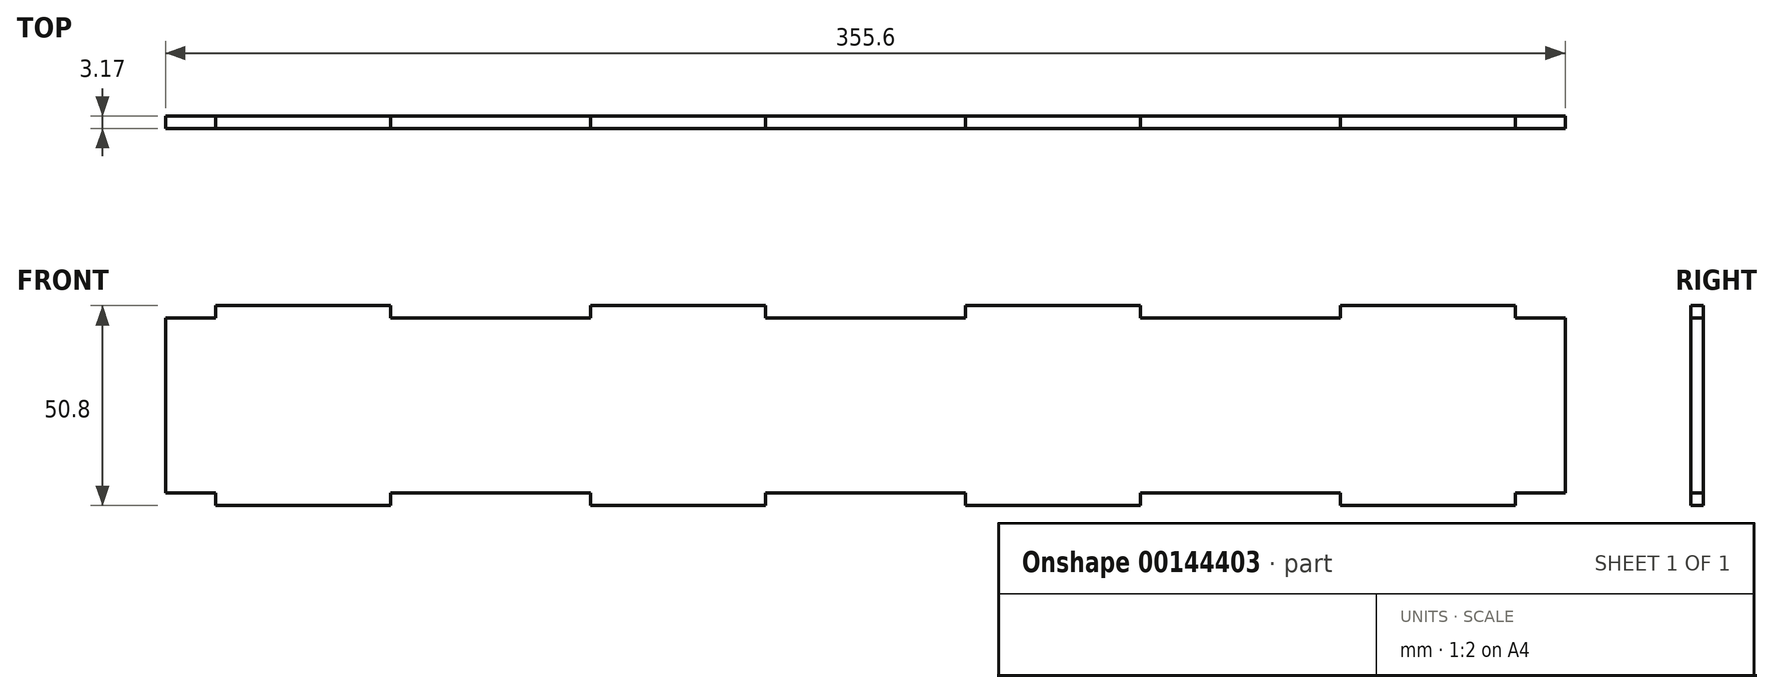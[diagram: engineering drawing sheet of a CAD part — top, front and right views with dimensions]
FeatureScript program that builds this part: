
annotation { "Feature Type Name" : "Feature", "Feature Type Description" : "" }
export const myFeature = defineFeature(function(context is Context, id is Id, definition is map)
    precondition{}
    {
        {
            var Q0;
            Q0=qCreatedBy(makeId("Front.planeOp"),FACE);
            var sketch = newSketch(context, id + "F0", { "sketchPlane" : qUnion([Q0])});
            skLineSegment(sketch, "E0", {"start": v(12.7, 0) * mm, "end": v(57.15, 0) * mm});
            skLineSegment(sketch, "E1", {"start": v(177.8, 3.18) * mm, "end": v(177.8, 47.62) * mm});
            skLineSegment(sketch, "E2", {"start": v(152.4, 50.8) * mm, "end": v(107.95, 50.8) * mm});
            skLineSegment(sketch, "E3", {"start": v(0, 47.62) * mm, "end": v(0, 3.18) * mm});
            skLineSegment(sketch, "E4.top", {"start": v(0, 47.62) * mm, "end": v(12.7, 47.62) * mm});
            skLineSegment(sketch, "E4.right", {"start": v(12.7, 50.8) * mm, "end": v(12.7, 47.62) * mm});
            skLineSegment(sketch, "E5.top", {"start": v(177.8, 47.62) * mm, "end": v(152.4, 47.62) * mm});
            skLineSegment(sketch, "E5.right", {"start": v(152.4, 50.8) * mm, "end": v(152.4, 47.62) * mm});
            skLineSegment(sketch, "E6.top", {"start": v(57.15, 47.62) * mm, "end": v(107.95, 47.62) * mm});
            skLineSegment(sketch, "E6.left", {"start": v(57.15, 50.8) * mm, "end": v(57.15, 47.62) * mm});
            skLineSegment(sketch, "E6.right", {"start": v(107.95, 50.8) * mm, "end": v(107.95, 47.62) * mm});
            skLineSegment(sketch, "E7", {"start": v(0, 25.4) * mm, "end": v(177.8, 25.4) * mm});
            skLineSegment(sketch, "E8.MirrorCS", {"start": v(0, 3.17) * mm, "end": v(12.7, 3.17) * mm});
            skLineSegment(sketch, "E9.MirrorCS", {"start": v(12.7, 0) * mm, "end": v(12.7, 3.18) * mm});
            skLineSegment(sketch, "E10.MirrorCS", {"start": v(57.15, 0) * mm, "end": v(57.15, 3.17) * mm});
            skLineSegment(sketch, "E11.MirrorCS", {"start": v(57.15, 3.17) * mm, "end": v(107.95, 3.18) * mm});
            skLineSegment(sketch, "E12.MirrorCS", {"start": v(107.95, 0) * mm, "end": v(107.95, 3.17) * mm});
            skLineSegment(sketch, "E13.MirrorCS", {"start": v(152.4, 0) * mm, "end": v(152.4, 3.17) * mm});
            skLineSegment(sketch, "E14.MirrorCS", {"start": v(177.8, 3.18) * mm, "end": v(152.4, 3.18) * mm});
            skPoint(sketch, "E15.orphan", {"position": v(0, 0) * mm});
            skPoint(sketch, "E16.orphan", {"position": v(0, 50.8) * mm});
            skLineSegment(sketch, "E17.trimOffspring", {"start": v(107.95, 0) * mm, "end": v(152.4, 0) * mm});
            skLineSegment(sketch, "E18.trimOffspring", {"start": v(57.15, 50.8) * mm, "end": v(12.7, 50.8) * mm});
            skPoint(sketch, "E19.orphan", {"position": v(177.8, 50.8) * mm});
            skPoint(sketch, "E20.orphan", {"position": v(177.8, 0) * mm});
            skLineSegment(sketch, "E21.MirrorCS", {"start": v(342.9, 0) * mm, "end": v(342.9, 3.18) * mm});
            skLineSegment(sketch, "E22.MirrorCS", {"start": v(203.2, 0) * mm, "end": v(203.2, 3.17) * mm});
            skLineSegment(sketch, "E23.MirrorCS", {"start": v(298.45, 0) * mm, "end": v(298.45, 3.17) * mm});
            skLineSegment(sketch, "E24.MirrorCS", {"start": v(247.65, 50.8) * mm, "end": v(247.65, 47.62) * mm});
            skLineSegment(sketch, "E25.MirrorCS", {"start": v(298.45, 50.8) * mm, "end": v(298.45, 47.62) * mm});
            skLineSegment(sketch, "E26.MirrorCS", {"start": v(203.2, 50.8) * mm, "end": v(203.2, 47.62) * mm});
            skLineSegment(sketch, "E27.MirrorCS", {"start": v(342.9, 50.8) * mm, "end": v(342.9, 47.62) * mm});
            skLineSegment(sketch, "E28.MirrorCS", {"start": v(247.65, 0) * mm, "end": v(247.65, 3.17) * mm});
            skLineSegment(sketch, "E29.MirrorCS", {"start": v(342.9, 0) * mm, "end": v(298.45, 0) * mm});
            skLineSegment(sketch, "E30.MirrorCS", {"start": v(298.45, 3.17) * mm, "end": v(247.65, 3.18) * mm});
            skLineSegment(sketch, "E31.MirrorCS", {"start": v(203.2, 50.8) * mm, "end": v(247.65, 50.8) * mm});
            skLineSegment(sketch, "E32.MirrorCS", {"start": v(355.6, 47.62) * mm, "end": v(355.6, 3.18) * mm});
            skLineSegment(sketch, "E33.MirrorCS", {"start": v(355.6, 47.62) * mm, "end": v(342.9, 47.62) * mm});
            skLineSegment(sketch, "E34.MirrorCS", {"start": v(355.6, 25.4) * mm, "end": v(177.8, 25.4) * mm});
            skLineSegment(sketch, "E35.MirrorCS", {"start": v(298.45, 50.8) * mm, "end": v(342.9, 50.8) * mm});
            skLineSegment(sketch, "E36.MirrorCS", {"start": v(355.6, 3.17) * mm, "end": v(342.9, 3.17) * mm});
            skLineSegment(sketch, "E37.MirrorCS", {"start": v(177.8, 3.18) * mm, "end": v(203.2, 3.18) * mm});
            skPoint(sketch, "E38.MirrorP", {"position": v(355.6, 50.8) * mm});
            skLineSegment(sketch, "E39.MirrorCS", {"start": v(298.45, 47.62) * mm, "end": v(247.65, 47.62) * mm});
            skPoint(sketch, "E40.MirrorP", {"position": v(355.6, 0) * mm});
            skLineSegment(sketch, "E41.MirrorCS", {"start": v(177.8, 47.62) * mm, "end": v(203.2, 47.62) * mm});
            skLineSegment(sketch, "E42.MirrorCS", {"start": v(247.65, 0) * mm, "end": v(203.2, 0) * mm});
            skSolve(sketch);
        }
        {
            var Q0;
            Q0=qSketchRegion(id+"F0",true);
            extrude(context, id + "F1", {"entities" : qUnion([Q0]), "depth" : 3.17 * mm});
        }
    });
